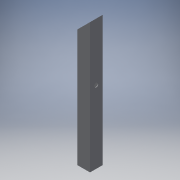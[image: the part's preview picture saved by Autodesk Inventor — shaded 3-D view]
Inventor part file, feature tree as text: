
AUTODESK INVENTOR PART (.ipt)
format: ipt  version: 2018 (Build 220112000, 112)  size: 115,712 bytes
history: native  units: mm
features: sketch x2, extrude x1, hole x1, chamfer x1
ambient origin geometry x8: Origin, YZ Plane, XZ Plane, XY Plane, X Axis, Y Axis, Z Axis, Center Point
bodies: Body1 (feature_tree)
feature tree (5):
  extrude  "押し出し3"  Depth=32.0mm
  hole  "穴1"  [1 undecoded]
  chamfer  "面取り2"  Distance=1.6mm
  sketch  "スケッチ1"
  sketch  "スケッチ7"
note: 1 required parameter value undecoded (feature->parameter linkage not recoverable at this tier; creation-order binding heuristic only, values carry confidence <= 0.55)
